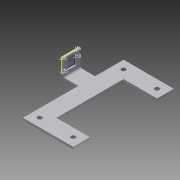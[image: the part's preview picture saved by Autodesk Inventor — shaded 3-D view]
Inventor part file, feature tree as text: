
AUTODESK INVENTOR PART (.ipt)
format: ipt  version: 2013 (Build 170138000, 138)  size: 245,248 bytes
history: native  units: in
note: dims shown in document units (in); Inventor stores cm internally (conversion verified against a paired STEP export)
features: sheet_metal_op x8, other x8, sketch x7
ambient origin geometry x8: Origin, YZ Plane, XZ Plane, XY Plane, X Axis, Y Axis, Z Axis, Center Point
bodies: Solid1 (feature_tree)
feature tree (23):
  sheet_metal_op  "Face1"
  sheet_metal_op  "Flange1"
  sheet_metal_op  "Face2"
  sketch  "Sketch4"  dims[d4=0.125in]
  sheet_metal_op  "Face3"
  sketch  "Sketch1"  dims[d0=1.0in]
  other  "Plate1"
  sketch  "Sketch2"  dims[d2=1.0in]
  other  "Plate2"
  sheet_metal_op  "Bend1"
  sheet_metal_op  "Corner1"
  sketch  "Sketch3"  dims[d3=0.125in]
  other  "Plate3"
  sheet_metal_op  "Bend2"
  sketch  "Sketch5"  dims[d5=0.0625in]
  sketch  "Sketch6"  dims[d6=0.25in]
  other  "Plate4"
  sheet_metal_op  "Bend3"
  sketch  "Sketch7"  dims[d7=0.125in d8=1.0in d9=90.0deg d10=0.125in d11=0.5in d12=0.125in d13=0.125in d14=3.3in d15=1.0in d16=6.0in d17=0.125in d18=0.125in d19=0.0625in d20=0.25in d21=0.125in d27=0.266in d28=0.5in d29=0.5in d30=0.266in d31=0.5in d32=0.5in d33=0.125in d34=0.0in d35=2.0in d36=1.0in d37=1.0in d38=2.0in d39=1.0in d40=2.0in d41=2.0in d42=1.0in d43=2.0in d44=2.0in d45=1.0in d46=0.266in d47=0.266in d48=0.266in d49=0.266in d50=0.5in d51=0.5in d52=0.5in d53=0.5in d54=0.5in d55=0.5in d56=0.5in d57=0.5in d58=0.125in d59=0.125in d60=0.0625in d61=0.25in d62=0.125in d63=0.25in d64=0.25in d65=0.125in d66=0.125in d67=0.125in d68=0.0in d69=0.125in d70=0.0in]
  other  "Cut2"
  other  "Cut3"
  other  "Cut4"
  other  "Definition1"
